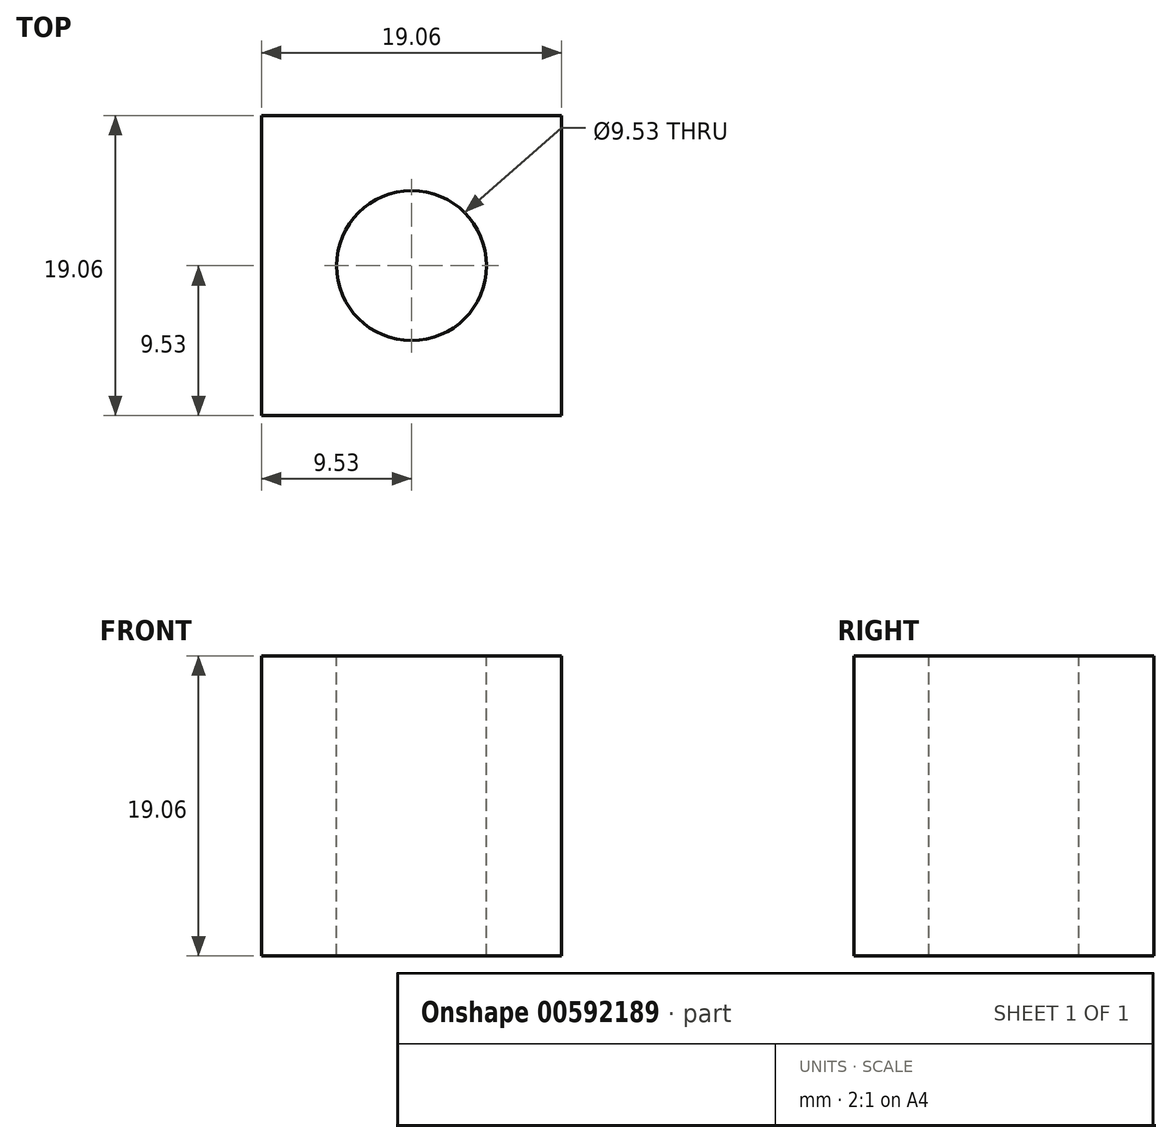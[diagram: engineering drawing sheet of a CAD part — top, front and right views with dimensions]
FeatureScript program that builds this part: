
annotation { "Feature Type Name" : "Feature", "Feature Type Description" : "" }
export const myFeature = defineFeature(function(context is Context, id is Id, definition is map)
    precondition{}
    {
        {
            var Q0;
            Q0=qCreatedBy(makeId("Front.planeOp"),FACE);
            var sketch = newSketch(context, id + "F0", { "sketchPlane" : qUnion([Q0])});
            skCircle(sketch, "E0", {"center": v(0, 0) * mm, "radius": 4.76 * mm});
            skLineSegment(sketch, "E1.bottom", {"start": v(9.53, 9.53) * mm, "end": v(-9.53, 9.53) * mm});
            skLineSegment(sketch, "E1.top", {"start": v(9.53, -9.53) * mm, "end": v(-9.53, -9.53) * mm});
            skLineSegment(sketch, "E1.left", {"start": v(9.53, 9.53) * mm, "end": v(9.53, -9.53) * mm});
            skLineSegment(sketch, "E1.right", {"start": v(-9.53, 9.53) * mm, "end": v(-9.53, -9.53) * mm});
            skLineSegment(sketch, "E2", {"start": v(0, 0) * mm, "end": v(9.53, 0) * mm, "construction": true});
            skSolve(sketch);
        }
        {
            var Q0;
            Q0 = qSketchRegion(id + "F0", true);
            extrude(context, id + "F1", {"entities" : qUnion([Q0]), "depth" : 19.05 * mm, "offsetDistance" : 25.4 * mm, "symmetric" : true});
        }
        {
            var Q0;
            Q0=makeQuery(id+"F1.opExtrude","SWEPT_BODY",BODY,{"disambiguationData":[OSD([sQuery(id+"F0.wireOp",EDGE,"E0"),sQuery(id+"F0.wireOp",EDGE,"E1.bottom"),sQuery(id+"F0.wireOp",EDGE,"E1.top"),sQuery(id+"F0.wireOp",EDGE,"E1.left"),sQuery(id+"F0.wireOp",EDGE,"E1.right")])]});
            var Q1;
            Q1=sQuery(id+"F0.wireOp",EDGE,"E2");
            transform(context, id + "F2", {"entities" : qUnion([Q0]), "transformType" : TransformType.ROTATION, "transformAxis" : qUnion([Q1]), "angle" : 90 * degree, "makeCopy" : false});
        }
    });
